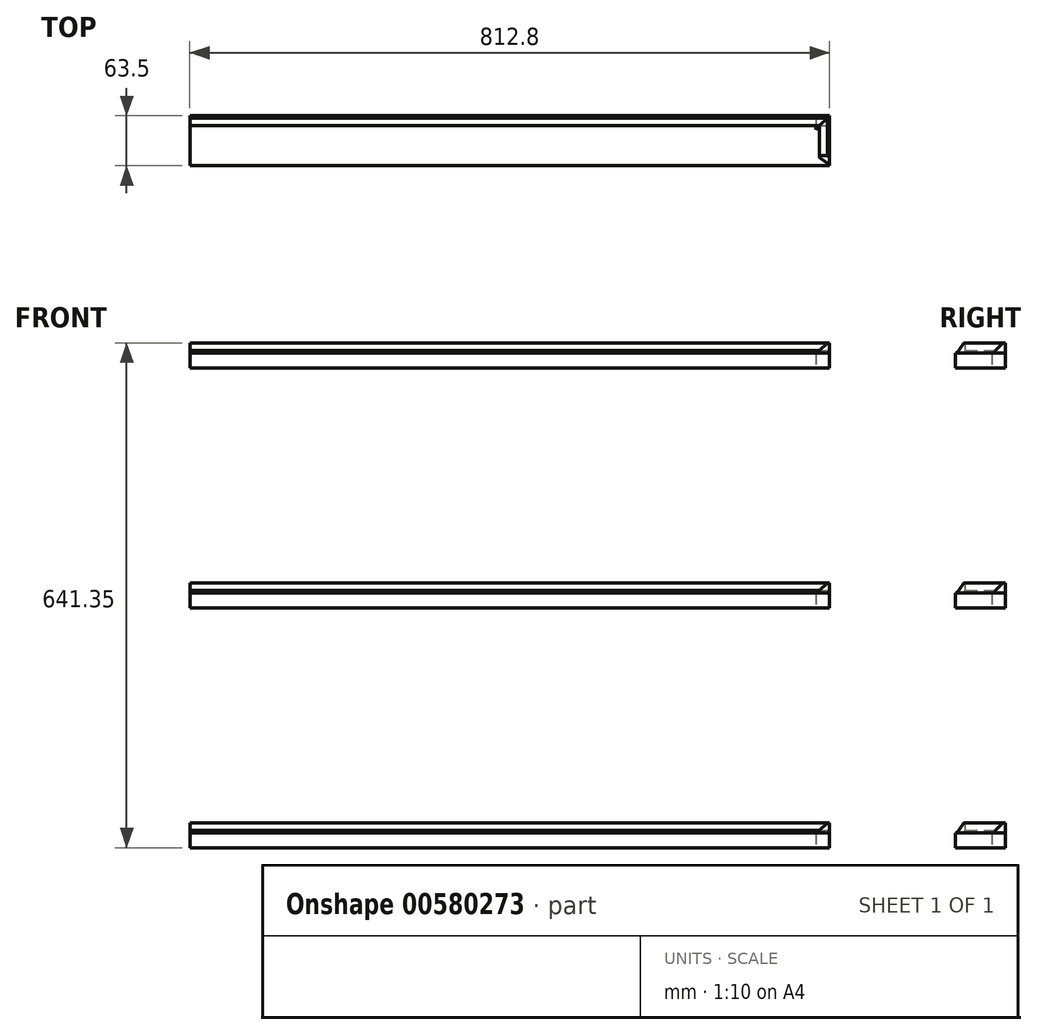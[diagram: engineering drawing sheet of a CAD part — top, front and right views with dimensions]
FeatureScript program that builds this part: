
annotation { "Feature Type Name" : "Feature", "Feature Type Description" : "" }
export const myFeature = defineFeature(function(context is Context, id is Id, definition is map)
    precondition{}
    {
        {
            var Q0;
            Q0=qCreatedBy(makeId("Top.planeOp"),FACE);
            var sketch = newSketch(context, id + "F0", { "sketchPlane" : qUnion([Q0])});
            skLineSegment(sketch, "E0", {"start": v(-389.6, 0) * mm, "end": v(-389.6, 76.2) * mm});
            skLineSegment(sketch, "E1", {"start": v(-389.6, 76.2) * mm, "end": v(423.2, 76.2) * mm});
            skLineSegment(sketch, "E2", {"start": v(423.2, 76.2) * mm, "end": v(423.2, 0) * mm});
            skLineSegment(sketch, "E3", {"start": v(423.2, 0) * mm, "end": v(524.8, 0) * mm});
            skLineSegment(sketch, "E4", {"start": v(-389.6, 0) * mm, "end": v(-516.6, 0) * mm});
            skSolve(sketch);
        }
        {
            var Q0;
            Q0 = qSketchRegion(id + "F0", true);
            var Q1;
            Q1=sQuery(id+"F0.wireOp",EDGE,"E1");
            var Q2;
            Q2=sQuery(id+"F0.wireOp",EDGE,"E0");
            var Q3;
            Q3=sQuery(id+"F0.wireOp",EDGE,"E4");
            var Q4;
            Q4=sQuery(id+"F0.wireOp",EDGE,"E2");
            var Q5;
            Q5=sQuery(id+"F0.wireOp",EDGE,"E3");
            extrude(context, id + "F1", {"entities" : qUnion([Q0]), "bodyType" : ToolBodyType.SURFACE, "surfaceEntities" : qUnion([Q1, Q2, Q3, Q4, Q5]), "depth" : 1828.8 * mm, "offsetDistance" : 25.4 * mm});
        }
        {
            var Q0;
            Q0=makeQuery(id+"F1.opExtrude","SWEPT_FACE",FACE,{"disambiguationData":[OSD([sQuery(id+"F0.wireOp",EDGE,"E1")])]});
            var sketch = newSketch(context, id + "F2", { "sketchPlane" : qUnion([Q0])});
            skLineSegment(sketch, "E5.bottom", {"start": v(-389.6, 1352.55) * mm, "end": v(423.2, 1352.55) * mm});
            skLineSegment(sketch, "E5.top", {"start": v(-389.6, 1371.6) * mm, "end": v(423.2, 1371.6) * mm});
            skLineSegment(sketch, "E5.left", {"start": v(-389.6, 1371.6) * mm, "end": v(-389.6, 1352.55) * mm});
            skLineSegment(sketch, "E5.right", {"start": v(423.2, 1371.6) * mm, "end": v(423.2, 1352.55) * mm});
            skLineSegment(sketch, "E6.bottom", {"start": v(-389.6, 1047.75) * mm, "end": v(423.2, 1047.75) * mm});
            skLineSegment(sketch, "E6.top", {"start": v(-389.6, 1066.8) * mm, "end": v(423.2, 1066.8) * mm});
            skLineSegment(sketch, "E6.left", {"start": v(-389.6, 1066.8) * mm, "end": v(-389.6, 1047.75) * mm});
            skLineSegment(sketch, "E6.right", {"start": v(423.2, 1066.8) * mm, "end": v(423.2, 1047.75) * mm});
            skLineSegment(sketch, "E7.bottom", {"start": v(-389.6, 742.95) * mm, "end": v(423.2, 742.95) * mm});
            skLineSegment(sketch, "E7.top", {"start": v(-389.6, 762) * mm, "end": v(423.2, 762) * mm});
            skLineSegment(sketch, "E7.left", {"start": v(-389.6, 762) * mm, "end": v(-389.6, 742.95) * mm});
            skLineSegment(sketch, "E7.right", {"start": v(423.2, 762) * mm, "end": v(423.2, 742.95) * mm});
            skSolve(sketch);
        }
        {
            var Q0;
            Q0 = qSketchRegion(id + "F2", true);
            extrude(context, id + "F3", {"entities" : qUnion([Q0]), "depth" : 63.5 * mm, "offsetDistance" : 25.4 * mm});
        }
        {
            var Q0;
            Q0=makeQuery(id+"F1.opExtrude","SWEPT_FACE",FACE,{"disambiguationData":[OSD([sQuery(id+"F0.wireOp",EDGE,"E1")])]});
            var sketch = newSketch(context, id + "F4", { "sketchPlane" : qUnion([Q0])});
            skLineSegment(sketch, "E8", {"start": v(423.2, 1371.6) * mm, "end": v(410.5, 1371.6) * mm});
            skLineSegment(sketch, "E9", {"start": v(410.5, 1371.6) * mm, "end": v(410.5, 1374.78) * mm});
            skLineSegment(sketch, "E10", {"start": v(410.5, 1374.78) * mm, "end": v(420.03, 1384.3) * mm});
            skLineSegment(sketch, "E11", {"start": v(420.03, 1384.3) * mm, "end": v(423.2, 1384.3) * mm});
            skLineSegment(sketch, "E12", {"start": v(423.2, 1384.3) * mm, "end": v(423.2, 1371.6) * mm});
            skLineSegment(sketch, "E13.direction1", {"start": v(410.5, 1371.6) * mm, "end": v(435.9, 1371.6) * mm, "construction": true});
            skLineSegment(sketch, "E14", {"start": v(423.2, 1066.8) * mm, "end": v(423.2, 1079.5) * mm});
            skLineSegment(sketch, "E15", {"start": v(423.2, 1079.5) * mm, "end": v(420.03, 1079.5) * mm});
            skLineSegment(sketch, "E16", {"start": v(420.03, 1079.5) * mm, "end": v(410.5, 1069.98) * mm});
            skLineSegment(sketch, "E17", {"start": v(410.5, 1069.98) * mm, "end": v(410.5, 1066.8) * mm});
            skLineSegment(sketch, "E18", {"start": v(410.5, 1066.8) * mm, "end": v(423.2, 1066.8) * mm});
            skLineSegment(sketch, "E19", {"start": v(423.2, 762) * mm, "end": v(423.2, 774.7) * mm});
            skLineSegment(sketch, "E20", {"start": v(420.03, 774.7) * mm, "end": v(423.2, 774.7) * mm});
            skLineSegment(sketch, "E21", {"start": v(420.03, 774.7) * mm, "end": v(410.5, 765.18) * mm});
            skLineSegment(sketch, "E22", {"start": v(410.5, 765.18) * mm, "end": v(410.5, 762) * mm});
            skLineSegment(sketch, "E23", {"start": v(410.5, 762) * mm, "end": v(423.2, 762) * mm});
            skSolve(sketch);
        }
        {
            var Q0;
            Q0 = qSketchRegion(id + "F4", true);
            extrude(context, id + "F5", {"entities" : qUnion([Q0]), "depth" : 63.5 * mm, "offsetDistance" : 25.4 * mm});
        }
        {
            var Q0;
            Q0=makeQuery(id+"F5.opExtrude","CAP_EDGE",EDGE,{"disambiguationData":[OSD([sQuery(id+"F4.wireOp",EDGE,"E16")])],"isStart":false});
            var Q1;
            Q1=makeQuery(id+"F5.opExtrude","CAP_EDGE",EDGE,{"disambiguationData":[OSD([sQuery(id+"F4.wireOp",EDGE,"E21")])],"isStart":false});
            var Q2;
            Q2=makeQuery(id+"F5.opExtrude","CAP_EDGE",EDGE,{"disambiguationData":[OSD([sQuery(id+"F4.wireOp",EDGE,"E10")])],"isStart":false});
            chamfer(context, id + "F6", {"entities" : qUnion([Q0, Q1, Q2]), "width" : 12.7 * mm, "tangentPropagation" : true});
        }
        {
            var Q0;
            Q0=makeQuery(id+"F3.opExtrude","SWEPT_FACE",FACE,{"disambiguationData":[OSD([sQuery(id+"F2.wireOp",EDGE,"E5.top")])]});
            var sketch = newSketch(context, id + "F7", { "sketchPlane" : qUnion([Q0])});
            skLineSegment(sketch, "E24", {"start": v(423.2, 76.2) * mm, "end": v(405.7, 58.7) * mm});
            skLineSegment(sketch, "E25", {"start": v(405.7, 58.7) * mm, "end": v(405.7, 80.52) * mm});
            skLineSegment(sketch, "E26", {"start": v(405.7, 80.52) * mm, "end": v(423.2, 80.52) * mm});
            skLineSegment(sketch, "E27", {"start": v(423.2, 80.52) * mm, "end": v(423.2, 76.2) * mm});
            skSolve(sketch);
        }
        {
            var Q0;
            Q0 = qSketchRegion(id + "F7", true);
            extrude(context, id + "F8", {"entities" : qUnion([Q0]), "operationType" : NewBodyOperationType.REMOVE, "depth" : 25.4 * mm, "offsetDistance" : 25.4 * mm, "hasSecondDirection" : true, "secondDirectionOppositeDirection" : true, "secondDirectionDepth" : 762 * mm});
        }
        {
            var Q0;
            Q0=makeQuery(id+"F1.opExtrude","SWEPT_FACE",FACE,{"disambiguationData":[OSD([sQuery(id+"F0.wireOp",EDGE,"E2")])]});
            var sketch = newSketch(context, id + "F9", { "sketchPlane" : qUnion([Q0])});
            skLineSegment(sketch, "E28", {"start": v(-76.2, 1371.6) * mm, "end": v(-76.2, 1384.3) * mm});
            skLineSegment(sketch, "E29", {"start": v(-76.2, 1384.3) * mm, "end": v(-73.02, 1384.3) * mm});
            skLineSegment(sketch, "E30", {"start": v(-73.02, 1384.3) * mm, "end": v(-63.5, 1374.77) * mm});
            skLineSegment(sketch, "E31", {"start": v(-63.5, 1374.77) * mm, "end": v(-63.5, 1371.6) * mm});
            skLineSegment(sketch, "E32", {"start": v(-63.5, 1371.6) * mm, "end": v(-76.2, 1371.6) * mm});
            skLineSegment(sketch, "E33.0.1.0", {"start": v(-76.2, 1066.8) * mm, "end": v(-76.2, 1079.5) * mm});
            skLineSegment(sketch, "E33.0.1.1", {"start": v(-76.2, 1079.5) * mm, "end": v(-73.02, 1079.5) * mm});
            skLineSegment(sketch, "E33.0.1.2", {"start": v(-73.02, 1079.5) * mm, "end": v(-63.5, 1069.97) * mm});
            skLineSegment(sketch, "E33.0.1.3", {"start": v(-63.5, 1069.97) * mm, "end": v(-63.5, 1066.8) * mm});
            skLineSegment(sketch, "E33.0.1.4", {"start": v(-63.5, 1066.8) * mm, "end": v(-76.2, 1066.8) * mm});
            skLineSegment(sketch, "E33.0.2.0", {"start": v(-76.2, 762) * mm, "end": v(-76.2, 774.7) * mm});
            skLineSegment(sketch, "E33.0.2.1", {"start": v(-76.2, 774.7) * mm, "end": v(-73.02, 774.7) * mm});
            skLineSegment(sketch, "E33.0.2.2", {"start": v(-73.02, 774.7) * mm, "end": v(-63.5, 765.17) * mm});
            skLineSegment(sketch, "E33.0.2.3", {"start": v(-63.5, 765.17) * mm, "end": v(-63.5, 762) * mm});
            skLineSegment(sketch, "E33.0.2.4", {"start": v(-63.5, 762) * mm, "end": v(-76.2, 762) * mm});
            skLineSegment(sketch, "E33.direction1", {"start": v(-76.2, 1371.6) * mm, "end": v(-50.8, 1371.6) * mm, "construction": true});
            skLineSegment(sketch, "E33.direction2", {"start": v(-76.2, 1371.6) * mm, "end": v(-76.2, 1066.8) * mm, "construction": true});
            skSolve(sketch);
        }
        {
            var Q0;
            Q0 = qSketchRegion(id + "F9", true);
            extrude(context, id + "F10", {"entities" : qUnion([Q0]), "depth" : 812.8 * mm, "offsetDistance" : 25.4 * mm});
        }
    });
